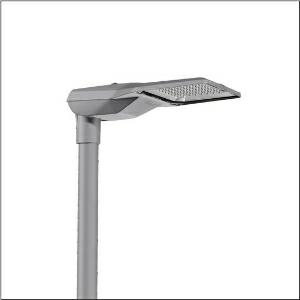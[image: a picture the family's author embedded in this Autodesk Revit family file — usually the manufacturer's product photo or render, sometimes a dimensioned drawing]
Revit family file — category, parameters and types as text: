
# Revit family: streetlight_sl_21_iq_midi___p0_8a_5xe3u31v08mb_d52e
name_source: partatom
category: Lighting Fixtures
units: mm (PartAtom-declared; Revit-internal decimal feet)

## family parameters
Cut with Voids When Loaded = No
Host = Face
Light Source = No
Part Type = Normal
Room Calculation Point = No
Round Connector Dimension = Use Diameter
Shared = No

## types (1)
- --- (1 x LED, 18500 lm, 129.3 W, 3000K)
    Apparent Load = 129 VA
    CIE Flux Codes = 33 69 96 100 100
    Color Rendering = 70
    Color Temperature = 3000K
    Default Elevation = 1800 mm
    Description = Streetlight SL 21 iQ midi, mast luminaire, primary light control with lens, of PMMA, primary optical cover: cover, of toughened safety glass, transparent, light distribution: P0.8a, light emission: direct distribution, primary light characteristic: asymmetric, installation type: post-top, side-entry, LED, High Power LED, rated luminous flux: 18.500lm, luminous efficacy: 143lm/W, light colour: 730, colour temperature: 3000K, control gear: iQ-Street Remote, D4i with power reduction, control: pre-setting: logarithmic dimming characteristic, Street-Remote, Auto-Match, Temp-Guard, Lumen-Switch, Night-Set, Smart-Wire, Light-Fading, Desk-Remote (wireless, voltage-free reading and setting of iQ features in the workshop via application-optimized NFC function/RFID function), optimised constant luminous flux control (CLO 2.0), mains connection: 230..240V, AC, 50/60Hz, start of lifetime: 129W, end of service life: 142W, reduction: 56W, luminaire housing, of diecast aluminium, powder-coated, Siteco® metallic grey (DB 702S), corrosivity category C5 mid according to DIN EN ISO 12944, please order mast flange separately, inclination adjustable: 0°, 5°, 10°, 15°, sealing non-destructively replaceable, multi-level sealing system, length: 644mm, width: 335mm, height: 110mm, mast flange for spigot size: 42mm (side-entry): 5XC10008XM4, 60/48mm (side-entry/post-top): 5XC10108XM2, 76/60mm (side-entry/post-top): 5XC10108XM1, mounting height: 4..8m, Smart Interface above, protection rating (complete): IP66, insulation class (complete): insulation class II (safety insulation), certification: CE, ENEC, ENEC+, VDE, impact resistance: IK10, permissible operating ambient temperature for outdoor applications: -40..+50°C, standard-compliant lighting for roads and squares, packaging unit: 1 piece

Light Distribution: P0.8a
    Height = 111 mm
    Lamp = 1 x LED
    Lamp Light Flux = 18500 lm
    Lamp Power = 129.3 W
    Lamp count = 1
    Length = 644 mm
    Luminous efficacy = 143 lm/W
    Manufacturer = Siteco
    ModVariant = No
    Model = 5XE3U31V08MB
    Number of Poles = 1
    OnlyDefault = Yes
    Power Factor = 1
    Product Name = Streetlight SL 21 iQ midi | P0.8a
    Product group = mast luminaire | pylon top
    ProductGroupID = 6100
    Protection Class = Protection class II
    Protection Degree = IP 66
    RLX_Detail_Level = 1
    RLX_Emergency_Light_Flux = 0 lm
    RLX_Emergency_Type = 0
    RLX_Emergency_Type_DB = No
    RlxData = <blob elided: 26849 chars, md5=445da160>
    Socket = socket
    Standby Power = 0 W
    System Light Flux = 18500 lm
    System Power = 129 W
    Type Comments = factory setting: luminous flux: 100 % | dim-lin: 254 | 672 mA
    Type Image = l_1004302.jpg
    URL = http://relux.com
    VarID = @adj_073946
    Voltage = 0 V
    Weight = 0.00 kg
    Width = 336 mm

## geometry (parser evidence)
native form markers: Blend x4, Sweep x12
no freeform markers — native parametric forms only
